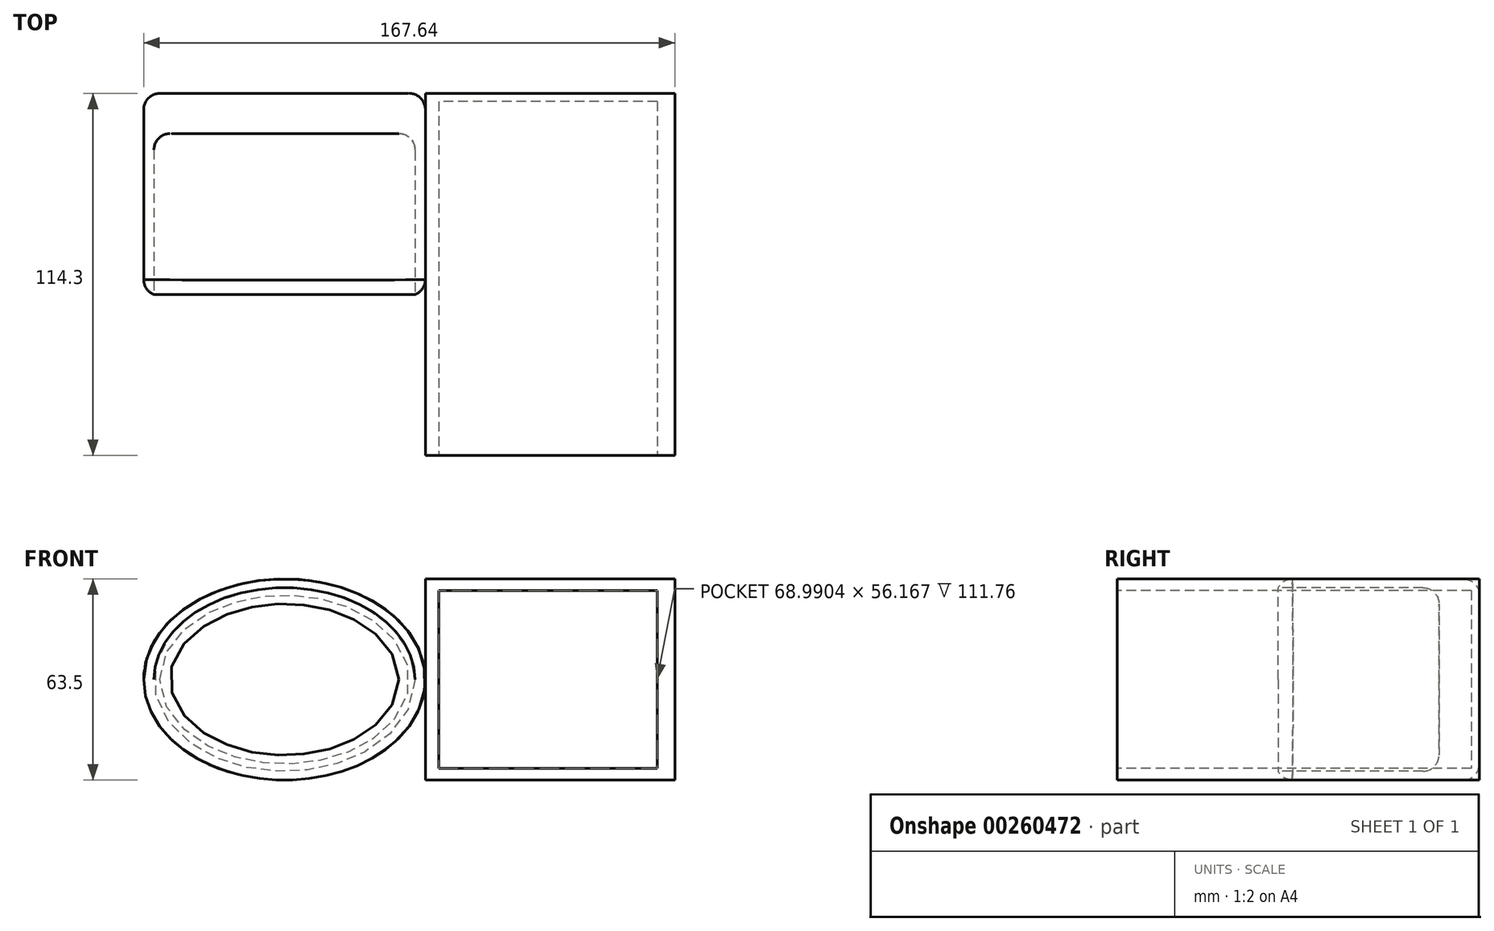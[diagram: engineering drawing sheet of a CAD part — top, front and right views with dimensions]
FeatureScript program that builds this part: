
annotation { "Feature Type Name" : "Feature", "Feature Type Description" : "" }
export const myFeature = defineFeature(function(context is Context, id is Id, definition is map)
    precondition{}
    {
        {
            var Q0;
            Q0=qCreatedBy(makeId("Front.planeOp"),FACE);
            var sketch = newSketch(context, id + "F0", { "sketchPlane" : qUnion([Q0])});
            skEllipse(sketch, "E0", {"center": v(0, 0) * mm, "majorRadius": 44.45 * mm, "minorRadius": 31.75 * mm, "majorAxis": v(-1, 0)});
            skPoint(sketch, "E1.endSnap0", {"position": v(44.45, 0) * mm});
            skLineSegment(sketch, "E2.bottom", {"start": v(44.45, 31.75) * mm, "end": v(123.2, 31.75) * mm});
            skLineSegment(sketch, "E2.top", {"start": v(44.45, -31.75) * mm, "end": v(123.2, -31.75) * mm});
            skLineSegment(sketch, "E2.right", {"start": v(123.2, 31.75) * mm, "end": v(123.2, -31.75) * mm});
            skLineSegment(sketch, "E3", {"start": v(0, -31.75) * mm, "end": v(44.45, -31.75) * mm});
            skLineSegment(sketch, "E4", {"start": v(0, 31.75) * mm, "end": v(44.45, 31.75) * mm});
            skLineSegment(sketch, "E5", {"start": v(44.45, 31.75) * mm, "end": v(44.45, -31.75) * mm});
            skSolve(sketch);
        }
        {
            var Q0;
            {var subQ0=sQuery(id+"F0.wireOp",EDGE,"E0");var subQ1=makeQuery(id+"F0.imprint","INTERSECT",VERTEX,{"derivedFrom":[subQ0,sQuery(id+"F0.wireOp",EDGE,"E3")]});Q0=makeQuery(id+"F0.imprint","IMPRINT",FACE,{"disambiguationData":[TD([[makeQuery(id+"F0.imprint","IMPRINT",EDGE,{"disambiguationData":[TD([[subQ1,-1.0]])],"derivedFrom":subQ0}),1.0]])]});}
            extrude(context, id + "F1", {"entities" : qUnion([Q0]), "depth" : 63.5 * mm});
        }
        {
            var Q0;
            Q0=makeQuery(id+"F1.opExtrude","CAP_FACE",FACE,{"disambiguationData":[OSD([sQuery(id+"F0.wireOp",EDGE,"E0")])],"isStart":false});
            var sketch = newSketch(context, id + "F2", { "sketchPlane" : qUnion([Q0])});
            skEllipse(sketch, "E6", {"center": v(0, 0) * mm, "majorRadius": 41.21 * mm, "minorRadius": 28.98 * mm, "majorAxis": v(1, 0)});
            skSolve(sketch);
        }
        {
            var Q0;
            Q0=makeQuery(id+"F2.imprint","IMPRINT",FACE,{"disambiguationData":[TD([[makeQuery(id+"F2.imprint","IMPRINT",EDGE,{"derivedFrom":sQuery(id+"F2.wireOp",EDGE,"E6")}),1.0]])]});
            extrude(context, id + "F3", {"entities" : qUnion([Q0]), "operationType" : NewBodyOperationType.REMOVE, "oppositeDirection" : true, "depth" : 50.8 * mm});
        }
        {
            var Q0;
            Q0=makeQuery(id+"F3.boolean.opBoolean","COPY",EDGE,{"derivedFrom":makeQuery(id+"F3.opExtrude","CAP_EDGE",EDGE,{"disambiguationData":[OSD([sQuery(id+"F2.wireOp",EDGE,"E6")])],"isStart":false})});
            fillet(context, id + "F4", {"entities" : qUnion([Q0]), "radius" : 5.08 * mm, "tangentPropagation" : true, "allowEdgeOverflow" : false});
        }
        {
            var Q0;
            {var subQ1=sQuery(id+"F0.wireOp",EDGE,"E2.bottom");Q0=makeQuery(id+"F0.imprint","IMPRINT",FACE,{"disambiguationData":[TD([[makeQuery(id+"F0.imprint","IMPRINT",EDGE,{"derivedFrom":subQ1}),-1.0]])]});}
            extrude(context, id + "F5", {"entities" : qUnion([Q0]), "operationType" : NewBodyOperationType.ADD, "depth" : 114.3 * mm});
        }
        {
            var Q0;
            Q0=makeQuery(id+"F1.opExtrude","SWEPT_FACE",FACE,{"disambiguationData":[OSD([sQuery(id+"F0.wireOp",EDGE,"E0")])]});
            fillet(context, id + "F6", {"entities" : qUnion([Q0]), "radius" : 5.08 * mm, "tangentPropagation" : true, "allowEdgeOverflow" : false});
        }
        {
            var Q0;
            Q0=makeQuery(id+"F5.opExtrude","CAP_FACE",FACE,{"disambiguationData":[OSD([sQuery(id+"F0.wireOp",EDGE,"E2.bottom"),sQuery(id+"F0.wireOp",EDGE,"E2.top"),sQuery(id+"F0.wireOp",EDGE,"E2.right"),sQuery(id+"F0.wireOp",EDGE,"E5")])],"isStart":false});
            var sketch = newSketch(context, id + "F7", { "sketchPlane" : qUnion([Q0])});
            skLineSegment(sketch, "E7.bottom", {"start": v(117.62, 28.08) * mm, "end": v(48.63, 28.08) * mm});
            skLineSegment(sketch, "E7.top", {"start": v(117.62, -28.08) * mm, "end": v(48.63, -28.08) * mm});
            skLineSegment(sketch, "E7.left", {"start": v(117.62, 28.08) * mm, "end": v(117.62, -28.08) * mm});
            skLineSegment(sketch, "E7.right", {"start": v(48.63, 28.08) * mm, "end": v(48.63, -28.08) * mm});
            skPoint(sketch, "E7.middle", {"position": v(83.13, 0) * mm});
            skSolve(sketch);
        }
        {
            var Q0;
            Q0=makeQuery(id+"F7.imprint","IMPRINT",FACE,{"disambiguationData":[TD([[makeQuery(id+"F7.imprint","IMPRINT",EDGE,{"derivedFrom":sQuery(id+"F7.wireOp",EDGE,"E7.bottom")}),1.0]])]});
            extrude(context, id + "F8", {"entities" : qUnion([Q0]), "operationType" : NewBodyOperationType.REMOVE, "oppositeDirection" : true, "depth" : 111.76 * mm});
        }
    });
